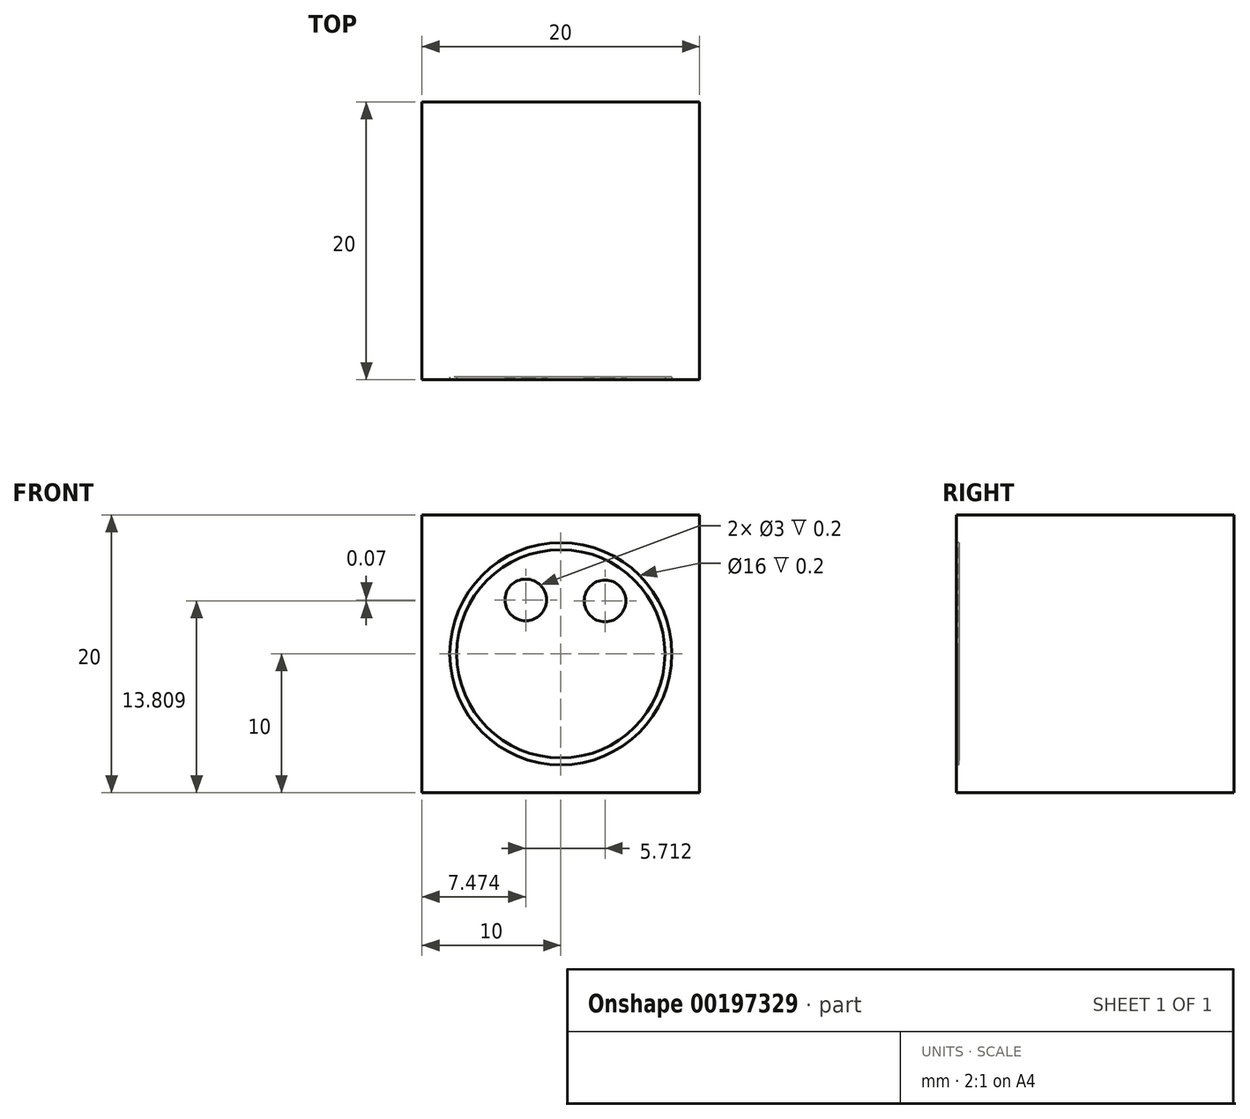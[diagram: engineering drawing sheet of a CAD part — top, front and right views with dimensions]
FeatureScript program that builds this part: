
annotation { "Feature Type Name" : "Feature", "Feature Type Description" : "" }
export const myFeature = defineFeature(function(context is Context, id is Id, definition is map)
    precondition{}
    {
        {
            var Q0;
            Q0=qCreatedBy(makeId("Front.planeOp"),FACE);
            var sketch = newSketch(context, id + "F0", { "sketchPlane" : qUnion([Q0])});
            skLineSegment(sketch, "E0.bottom", {"start": v(10, -10) * mm, "end": v(-10, -10) * mm});
            skLineSegment(sketch, "E0.top", {"start": v(10, 10) * mm, "end": v(-10, 10) * mm});
            skLineSegment(sketch, "E0.left", {"start": v(10, -10) * mm, "end": v(10, 10) * mm});
            skLineSegment(sketch, "E0.right", {"start": v(-10, -10) * mm, "end": v(-10, 10) * mm});
            skPoint(sketch, "E0.middle", {"position": v(0, 0) * mm});
            skSolve(sketch);
        }
        {
            var Q0;
            Q0 = qSketchRegion(id + "F0", true);
            extrude(context, id + "F1", {"entities" : qUnion([Q0]), "depth" : 20 * mm});
        }
        {
            var Q0;
            Q0=makeQuery(id+"F1.opExtrude","CAP_FACE",FACE,{"disambiguationData":[OSD([sQuery(id+"F0.wireOp",EDGE,"E0.bottom"),sQuery(id+"F0.wireOp",EDGE,"E0.top"),sQuery(id+"F0.wireOp",EDGE,"E0.left"),sQuery(id+"F0.wireOp",EDGE,"E0.right")])],"isStart":false});
            var sketch = newSketch(context, id + "F2", { "sketchPlane" : qUnion([Q0])});
            skCircle(sketch, "E1", {"center": v(0, 0) * mm, "radius": 8 * mm});
            skPoint(sketch, "E2", {"position": v(8, 0) * mm});
            skSolve(sketch);
        }
        {
            var Q0;
            Q0=sQuery(id+"F2.wireOp",VERTEX,"E2");
            var Q1;
            Q1=qCreatedBy(makeId("Origin.pointOp"),VERTEX);
            var Q2;
            Q2=sQuery(id+"F2.wireOp",VERTEX,"E1.center");
            cPlane(context, id + "F3", {"entities" : qUnion([Q0, Q1, Q2]), "cplaneType" : CPlaneType.THREE_POINT, "offset" : 25 * mm, "width" : 150 * mm, "height" : 150 * mm});
        }
        {
            var Q0;
            Q0=qCreatedBy(id+"F3.planeOp",FACE);
            var sketch = newSketch(context, id + "F4", { "sketchPlane" : qUnion([Q0])});
            skPoint(sketch, "E3.0", {"position": v(8, 20) * mm});
            skLineSegment(sketch, "E4.0", {"start": v(-8, 20) * mm, "end": v(8, 20) * mm});
            skLineSegment(sketch, "E5.bottom", {"start": v(8, 20) * mm, "end": v(7.5, 20) * mm});
            skLineSegment(sketch, "E5.top", {"start": v(8, 19.8) * mm, "end": v(7.5, 19.8) * mm});
            skLineSegment(sketch, "E5.left", {"start": v(8, 20) * mm, "end": v(8, 19.8) * mm});
            skLineSegment(sketch, "E5.right", {"start": v(7.5, 20) * mm, "end": v(7.5, 19.8) * mm});
            skSolve(sketch);
        }
        {
            var Q0;
            Q0 = qSketchRegion(id + "F4", true);
            var Q1;
            Q1 = qConstructionFilter(qBodyType(qCreatedBy(id + "F2" ,EDGE), BodyType.WIRE), ConstructionObject.NO);
            sweep(context, id + "F5", {"profiles" : qUnion([Q0]), "path" : qUnion([Q1])});
        }
        {
            var Q0;
            Q0 = qSketchRegion(id + "F4", true);
            var Q1;
            Q1 = qConstructionFilter(qBodyType(qCreatedBy(id + "F2" ,EDGE), BodyType.WIRE), ConstructionObject.NO);
            sweep(context, id + "F6", {"operationType" : NewBodyOperationType.REMOVE, "profiles" : qUnion([Q0]), "path" : qUnion([Q1])});
        }
        {
            var Q0;
            Q0=makeQuery(id+"F2.imprint","IMPRINT",FACE,{"disambiguationData":[TD([[makeQuery(id+"F2.imprint","IMPRINT",EDGE,{"derivedFrom":sQuery(id+"F2.wireOp",EDGE,"E1")}),1.0]])]});
            var sketch = newSketch(context, id + "F7", { "sketchPlane" : qUnion([Q0])});
            skCircle(sketch, "E6", {"center": v(-2.53, 3.88) * mm, "radius": 1.5 * mm});
            skCircle(sketch, "E7", {"center": v(3.19, 3.8) * mm, "radius": 1.5 * mm});
            skSolve(sketch);
        }
        {
            var Q0;
            Q0=makeQuery(id+"F7.imprint","IMPRINT",FACE,{"disambiguationData":[TD([[makeQuery(id+"F7.imprint","IMPRINT",EDGE,{"derivedFrom":sQuery(id+"F7.wireOp",EDGE,"E7")}),1.0]])]});
            var Q1;
            Q1=makeQuery(id+"F7.imprint","IMPRINT",FACE,{"disambiguationData":[TD([[makeQuery(id+"F7.imprint","IMPRINT",EDGE,{"derivedFrom":sQuery(id+"F7.wireOp",EDGE,"E6")}),1.0]])]});
            var Q2;
            Q2=sQuery(id+"F7.wireOp",EDGE,"E7");
            extrude(context, id + "F8", {"entities" : qUnion([Q0, Q1]), "operationType" : NewBodyOperationType.REMOVE, "surfaceEntities" : qUnion([Q2]), "oppositeDirection" : true, "depth" : .2 * mm});
        }
        {
            var Q0;
            Q0=makeQuery(id+"F7.imprint","IMPRINT",FACE,{"disambiguationData":[TD([[makeQuery(id+"F7.imprint","IMPRINT",EDGE,{"derivedFrom":sQuery(id+"F7.wireOp",EDGE,"E6")}),1.0]])]});
            var Q1;
            Q1=makeQuery(id+"F7.imprint","IMPRINT",FACE,{"disambiguationData":[TD([[makeQuery(id+"F7.imprint","IMPRINT",EDGE,{"derivedFrom":sQuery(id+"F7.wireOp",EDGE,"E7")}),1.0]])]});
            extrude(context, id + "F9", {"entities" : qUnion([Q0, Q1]), "oppositeDirection" : true, "depth" : .2 * mm});
        }
    });
